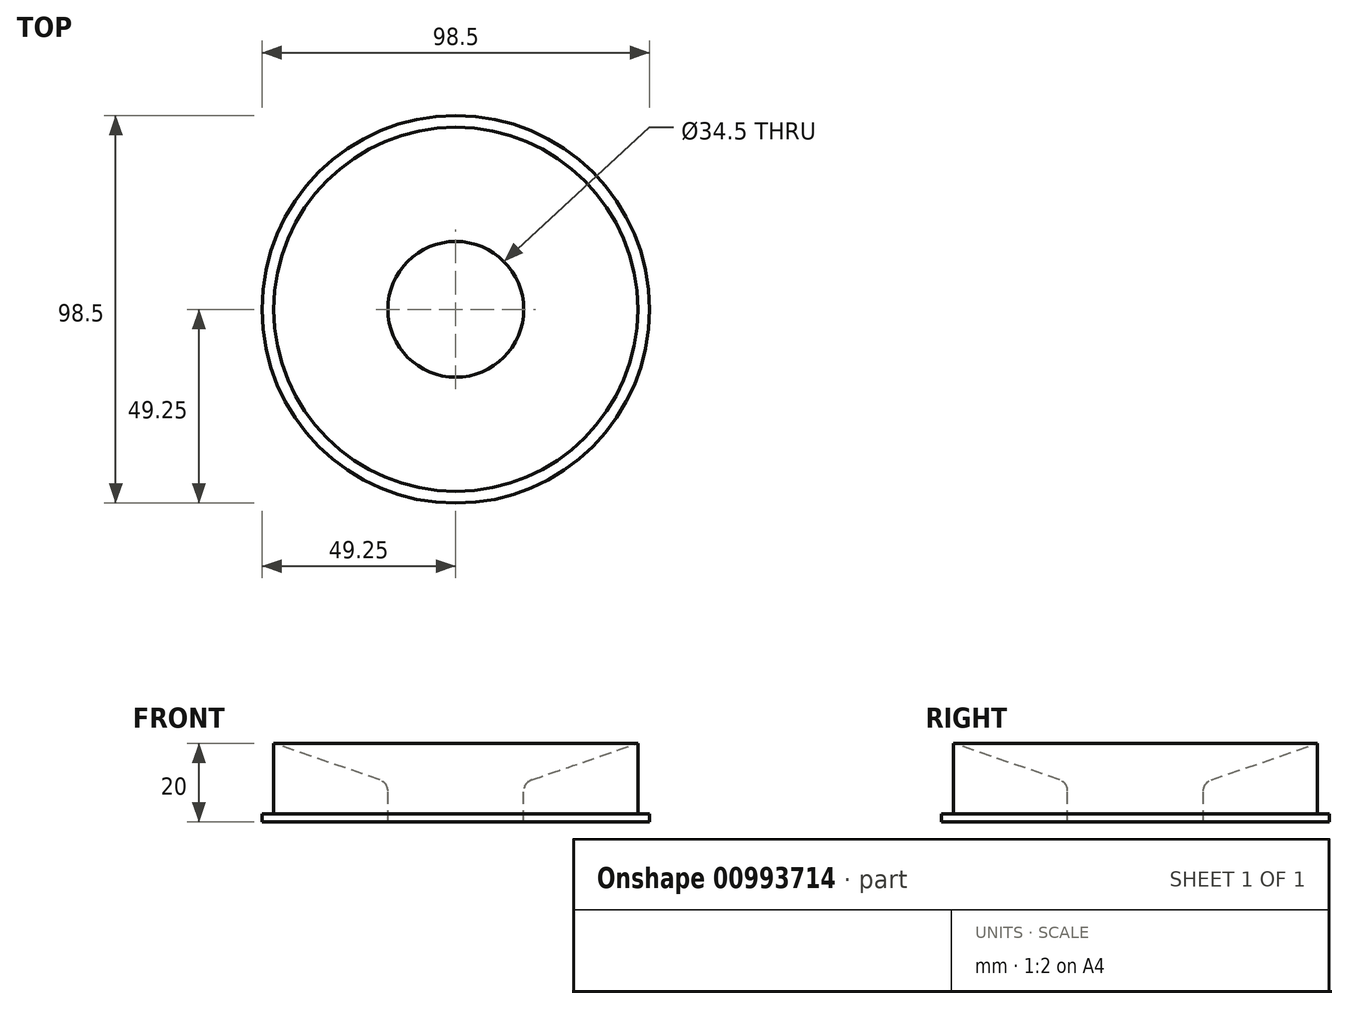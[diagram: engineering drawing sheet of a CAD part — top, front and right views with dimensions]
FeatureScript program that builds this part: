
annotation { "Feature Type Name" : "Feature", "Feature Type Description" : "" }
export const myFeature = defineFeature(function(context is Context, id is Id, definition is map)
    precondition{}
    {
        {
            var Q0;
            Q0=qCreatedBy(makeId("Front.planeOp"),FACE);
            var sketch = newSketch(context, id + "F0", { "sketchPlane" : qUnion([Q0])});
            skLineSegment(sketch, "E0", {"start": v(17.25, 0) * mm, "end": v(17.25, 7.86) * mm});
            skLineSegment(sketch, "E1", {"start": v(46.25, 2) * mm, "end": v(46.25, 20) * mm});
            skLineSegment(sketch, "E2", {"start": v(46.25, 20) * mm, "end": v(19.27, 10.7) * mm});
            skLineSegment(sketch, "E3", {"start": v(17.25, 0) * mm, "end": v(46.25, 0) * mm});
            skPoint(sketch, "E4.visualSharp", {"position": v(17.25, 10) * mm});
            skArc(sketch, "E4.filletArc", {"start": v(19.27, 10.7) * mm, "mid": v(17.8, 9.6) * mm, "end": v(17.25, 7.86) * mm});
            skLineSegment(sketch, "E5", {"start": v(0, 61.1) * mm, "end": v(0, -50.93) * mm, "construction": true});
            skLineSegment(sketch, "E6", {"start": v(46.25, 0) * mm, "end": v(49.25, 0) * mm});
            skLineSegment(sketch, "E7", {"start": v(49.25, 0) * mm, "end": v(49.25, 2) * mm});
            skLineSegment(sketch, "E8", {"start": v(49.25, 2) * mm, "end": v(46.25, 2) * mm});
            skSolve(sketch);
        }
        {
            var Q0;
            Q0=makeQuery(id+"F0.imprint","IMPRINT",FACE,{"disambiguationData":[TD([[makeQuery(id+"F0.imprint","IMPRINT",EDGE,{"derivedFrom":sQuery(id+"F0.wireOp",EDGE,"E0")}),-1.0]])]});
            var Q1;
            Q1=sQuery(id+"F0.wireOp",EDGE,"E5");
            revolve(context, id + "F1", {"surfaceOperationType" : NewSurfaceOperationType.NEW, "entities" : qUnion([Q0]), "axis" : qUnion([Q1]), "revolveType" : RevolveType.FULL});
        }
    });
